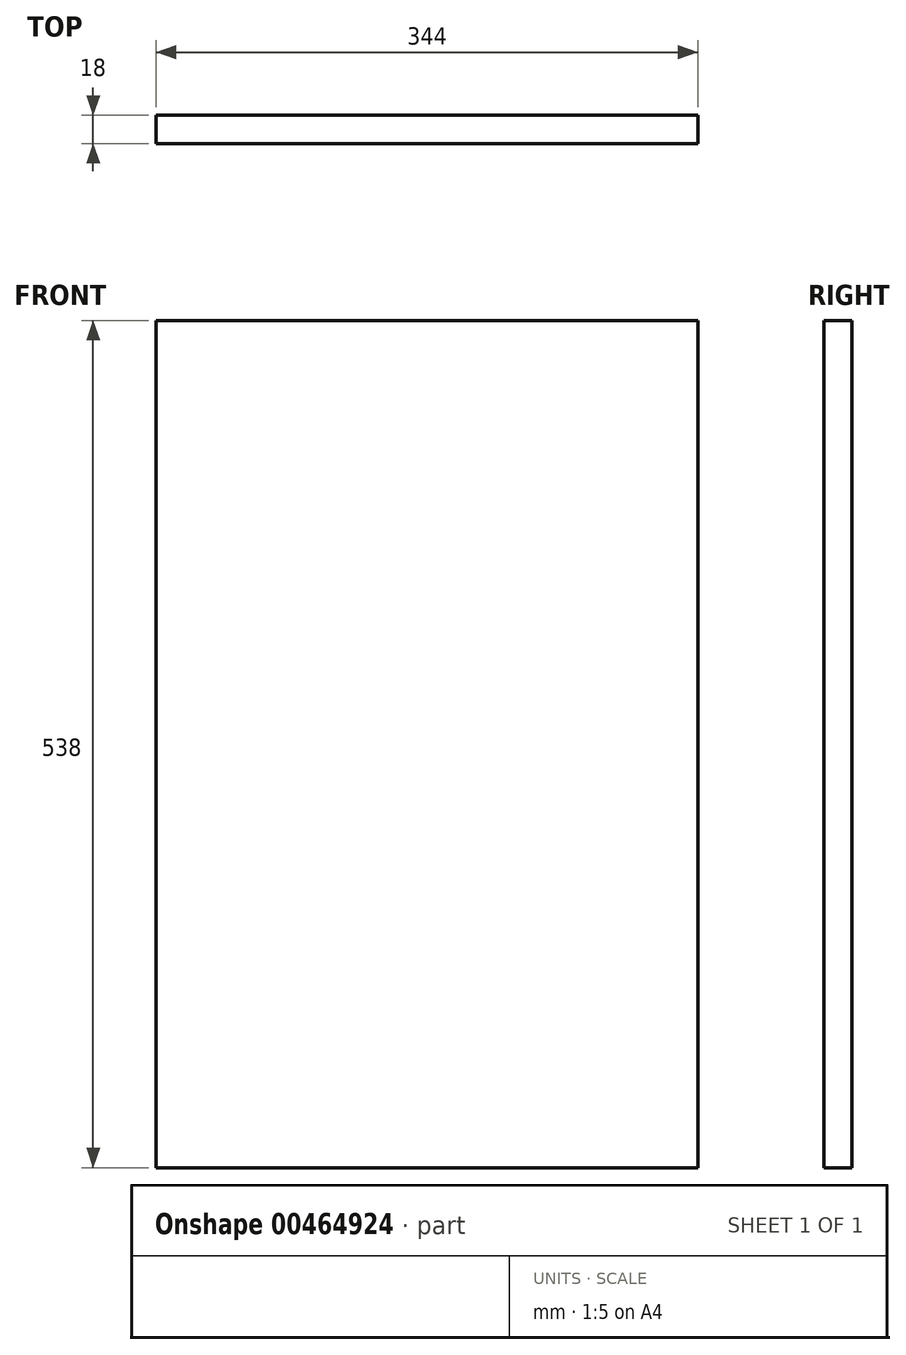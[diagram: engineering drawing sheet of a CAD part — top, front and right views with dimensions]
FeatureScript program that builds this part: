
annotation { "Feature Type Name" : "Feature", "Feature Type Description" : "" }
export const myFeature = defineFeature(function(context is Context, id is Id, definition is map)
    precondition{}
    {
        {
            var Q0;
            Q0=qCreatedBy(makeId("Front.planeOp"),FACE);
            var sketch = newSketch(context, id + "F0", { "sketchPlane" : qUnion([Q0])});
            skLineSegment(sketch, "E0.bottom", {"start": v(172, -269) * mm, "end": v(-172, -269) * mm});
            skLineSegment(sketch, "E0.top", {"start": v(172, 269) * mm, "end": v(-172, 269) * mm});
            skLineSegment(sketch, "E0.left", {"start": v(172, -269) * mm, "end": v(172, 269) * mm});
            skLineSegment(sketch, "E0.right", {"start": v(-172, -269) * mm, "end": v(-172, 269) * mm});
            skPoint(sketch, "E0.middle", {"position": v(0, 0) * mm});
            skSolve(sketch);
        }
        {
            var Q0;
            Q0=qSketchRegion(id+"F0",true);
            extrude(context, id + "F1", {"entities" : qUnion([Q0]), "depth" : 18 * mm, "offsetDistance" : 25 * mm});
        }
    });
